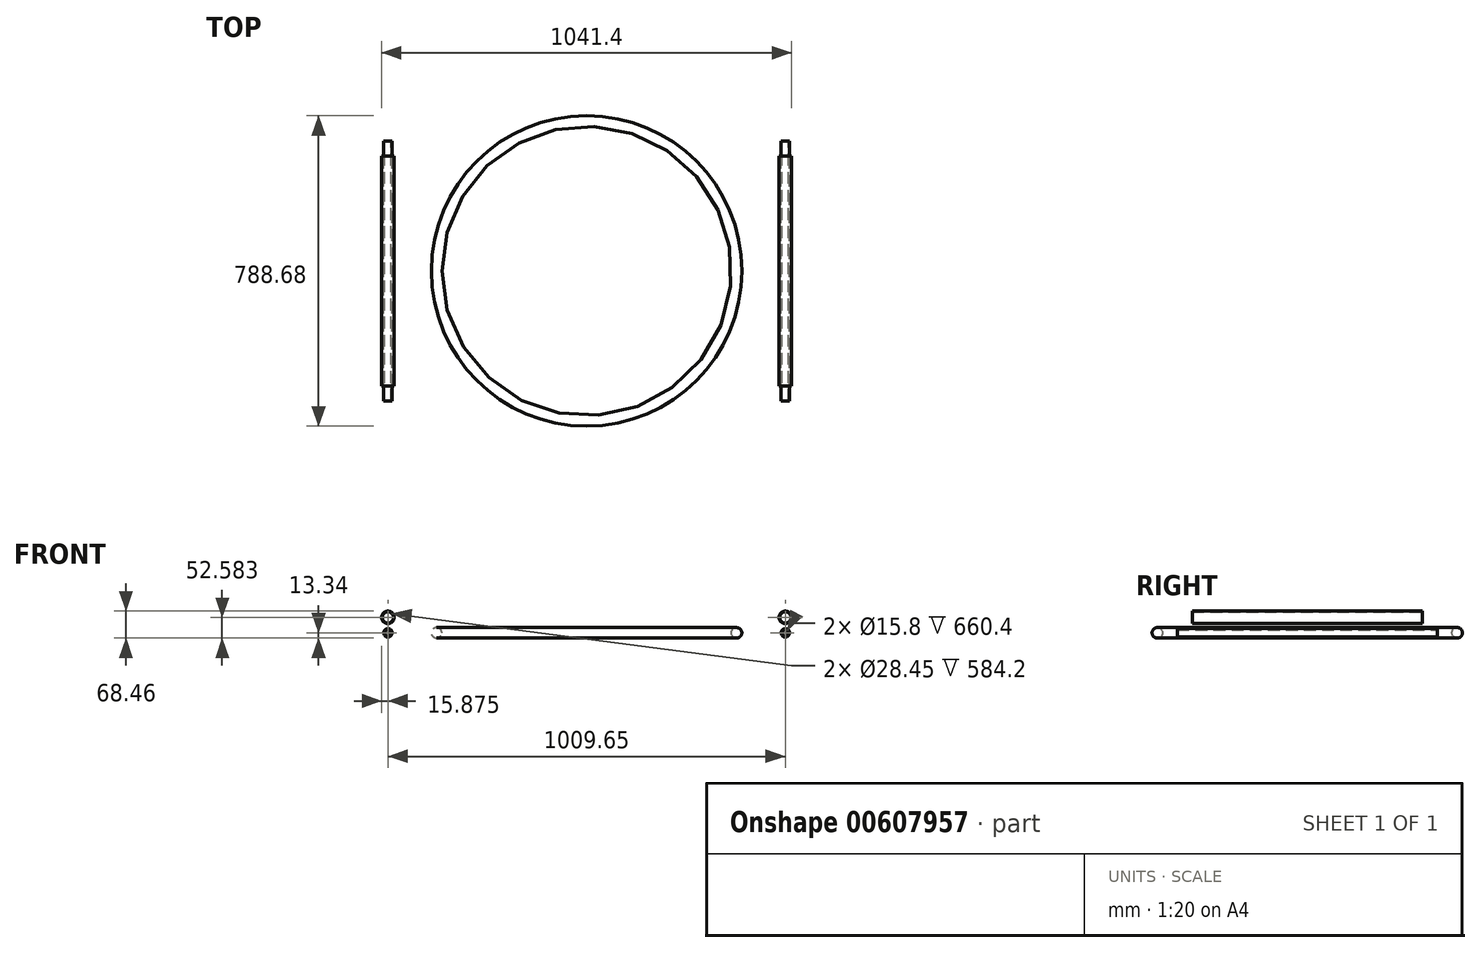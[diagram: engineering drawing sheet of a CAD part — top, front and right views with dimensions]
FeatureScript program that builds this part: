
annotation { "Feature Type Name" : "Feature", "Feature Type Description" : "" }
export const myFeature = defineFeature(function(context is Context, id is Id, definition is map)
    precondition{}
    {
        {
            var Q0;
            Q0=qCreatedBy(makeId("Front.planeOp"),FACE);
            var sketch = newSketch(context, id + "F0", { "sketchPlane" : qUnion([Q0])});
            skLineSegment(sketch, "E0.left", {"start": v(0, 0) * mm, "end": v(0, 20) * mm, "construction": true});
            skCircle(sketch, "E1", {"center": v(381, 0) * mm, "radius": 13.34 * mm});
            skCircle(sketch, "E2", {"center": v(381, 0) * mm, "radius": 10.5 * mm});
            skSolve(sketch);
        }
        {
            var Q0;
            Q0=makeQuery(id+"F0.imprint","IMPRINT",FACE,{"disambiguationData":[TD([[makeQuery(id+"F0.imprint","IMPRINT",EDGE,{"derivedFrom":sQuery(id+"F0.wireOp",EDGE,"E2")}),1.0]])]});
            var Q1;
            Q1=makeQuery(id+"F0.imprint","IMPRINT",FACE,{"disambiguationData":[TD([[makeQuery(id+"F0.imprint","IMPRINT",EDGE,{"derivedFrom":sQuery(id+"F0.wireOp",EDGE,"E1")}),1.0]])]});
            var Q2;
            Q2=sQuery(id+"F0.wireOp",EDGE,"E2");
            var Q3;
            Q3=sQuery(id+"F0.wireOp",EDGE,"E1");
            var Q4;
            Q4=sQuery(id+"F0.wireOp",EDGE,"E0.left");
            revolve(context, id + "F1", {"entities" : qUnion([Q0, Q1]), "surfaceEntities" : qUnion([Q2, Q3]), "axis" : qUnion([Q4]), "revolveType" : RevolveType.FULL});
        }
        {
            var Q0;
            Q0=qCreatedBy(makeId("Front.planeOp"),FACE);
            var sketch = newSketch(context, id + "F2", { "sketchPlane" : qUnion([Q0])});
            skCircle(sketch, "E3", {"center": v(504.82, 39.24) * mm, "radius": 15.88 * mm});
            skCircle(sketch, "E4.0", {"center": v(504.82, 39.24) * mm, "radius": 14.22 * mm});
            skSolve(sketch);
        }
        {
            var Q0;
            Q0 = qSketchRegion(id + "F2", true);
            extrude(context, id + "F3", {"entities" : qUnion([Q0]), "endBound" : BoundingType.SYMMETRIC, "depth" : 584.2 * mm, "offsetDistance" : 25 * mm});
        }
        {
            var Q0;
            Q0=qCreatedBy(makeId("Front.planeOp"),FACE);
            var sketch = newSketch(context, id + "F4", { "sketchPlane" : qUnion([Q0])});
            skCircle(sketch, "E5", {"center": v(504.82, 0) * mm, "radius": 7.9 * mm});
            skCircle(sketch, "E6", {"center": v(504.82, 0) * mm, "radius": 10.67 * mm});
            skSolve(sketch);
        }
        {
            var Q0;
            Q0 = qSketchRegion(id + "F4", true);
            extrude(context, id + "F5", {"entities" : qUnion([Q0]), "endBound" : BoundingType.SYMMETRIC, "depth" : 660.4 * mm, "offsetDistance" : 25 * mm});
        }
        {
            var Q0;
            Q0=makeQuery(id+"F3.opExtrude","SWEPT_BODY",BODY,{"disambiguationData":[OSD([sQuery(id+"F2.wireOp",EDGE,"E3"),sQuery(id+"F2.wireOp",EDGE,"E4.0")])]});
            var Q1;
            Q1=qCreatedBy(makeId("Right.planeOp"),FACE);
            mirror(context, id + "F6", {"entities" : qUnion([Q0]), "mirrorPlane" : qUnion([Q1])});
        }
        {
            var Q0;
            Q0=makeQuery(id+"F5.opExtrude","SWEPT_BODY",BODY,{"disambiguationData":[OSD([sQuery(id+"F4.wireOp",EDGE,"E5"),sQuery(id+"F4.wireOp",EDGE,"E6")])]});
            var Q1;
            Q1=qCreatedBy(makeId("Right.planeOp"),FACE);
            mirror(context, id + "F7", {"entities" : qUnion([Q0]), "mirrorPlane" : qUnion([Q1])});
        }
    });
